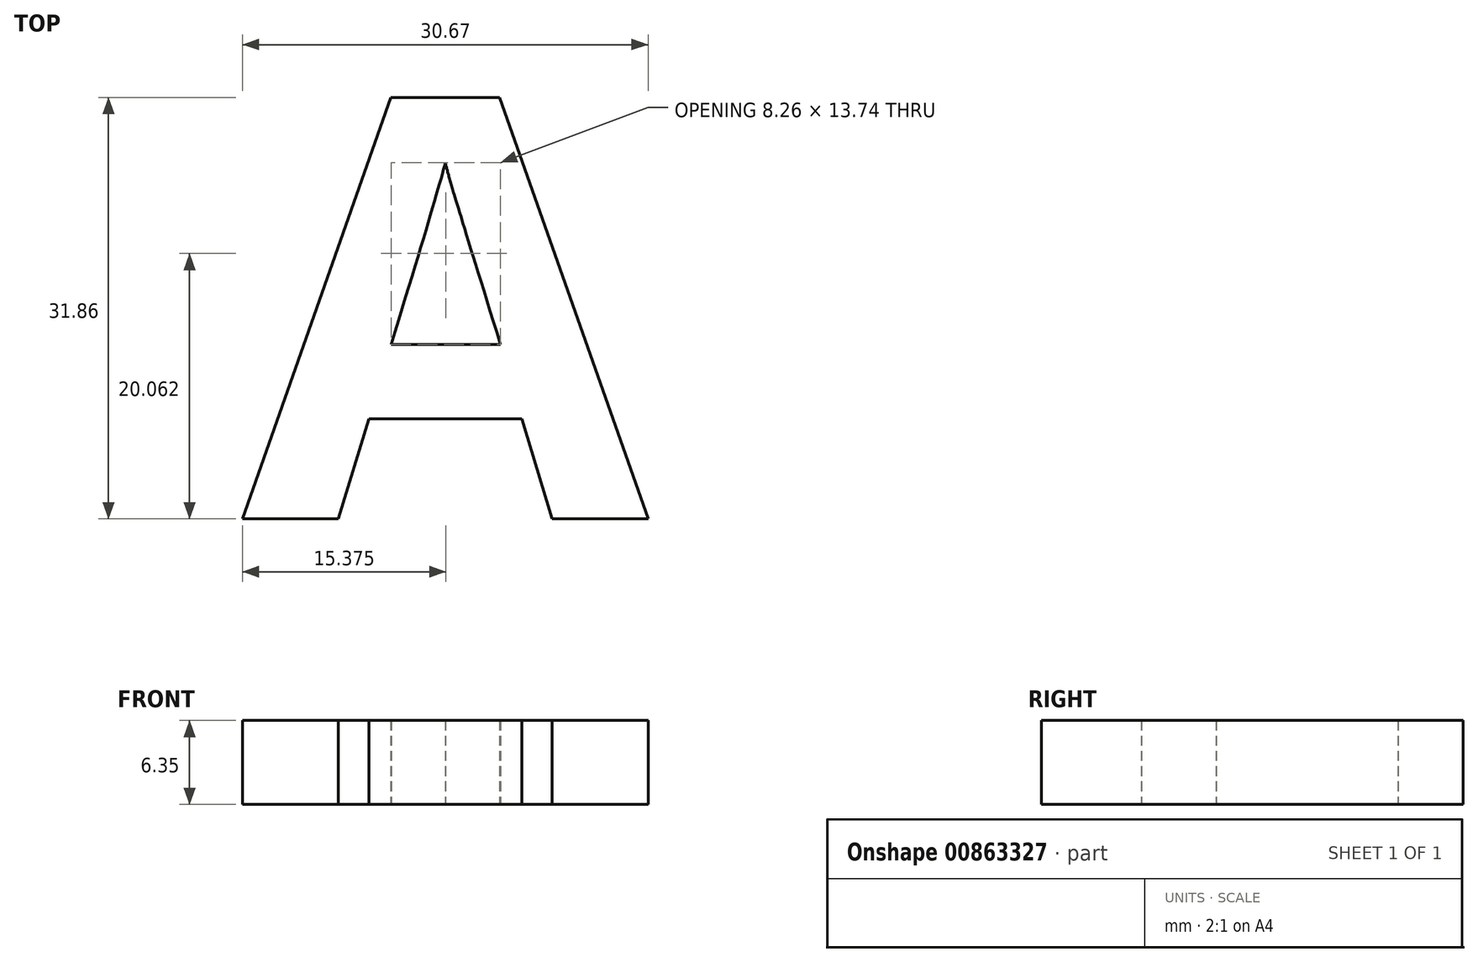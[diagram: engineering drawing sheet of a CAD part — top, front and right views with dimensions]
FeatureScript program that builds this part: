
annotation { "Feature Type Name" : "Feature", "Feature Type Description" : "" }
export const myFeature = defineFeature(function(context is Context, id is Id, definition is map)
    precondition{}
    {
        {
            var Q0;
            Q0=qCreatedBy(makeId("Top.planeOp"),FACE);
            var sketch = newSketch(context, id + "F0", { "sketchPlane" : qUnion([Q0])});
            skText(sketch, "E0", { "text": "A", "fontName": "OpenSans-Bold.ttf"});
            const initialGuessF0  = {"E0": [-0.01886, -0.00859, 1, 0, 0.032]};
            skSetInitialGuess(sketch, initialGuessF0);
            skSolve(sketch);
        }
        {
            var Q0;
            Q0=makeQuery(id+"F0.imprint","IMPRINT",FACE,{"disambiguationData":[TD([[makeQuery(id+"F0.imprint","IMPRINT",EDGE,{"derivedFrom":sQuery(id+"F0.wireOp",EDGE,"E0.sketch_text.stroke-0")}),-1.0]])]});
            extrude(context, id + "F1", {"entities" : qUnion([Q0]), "depth" : 6.35 * mm, "offsetDistance" : 25.4 * mm});
        }
    });
